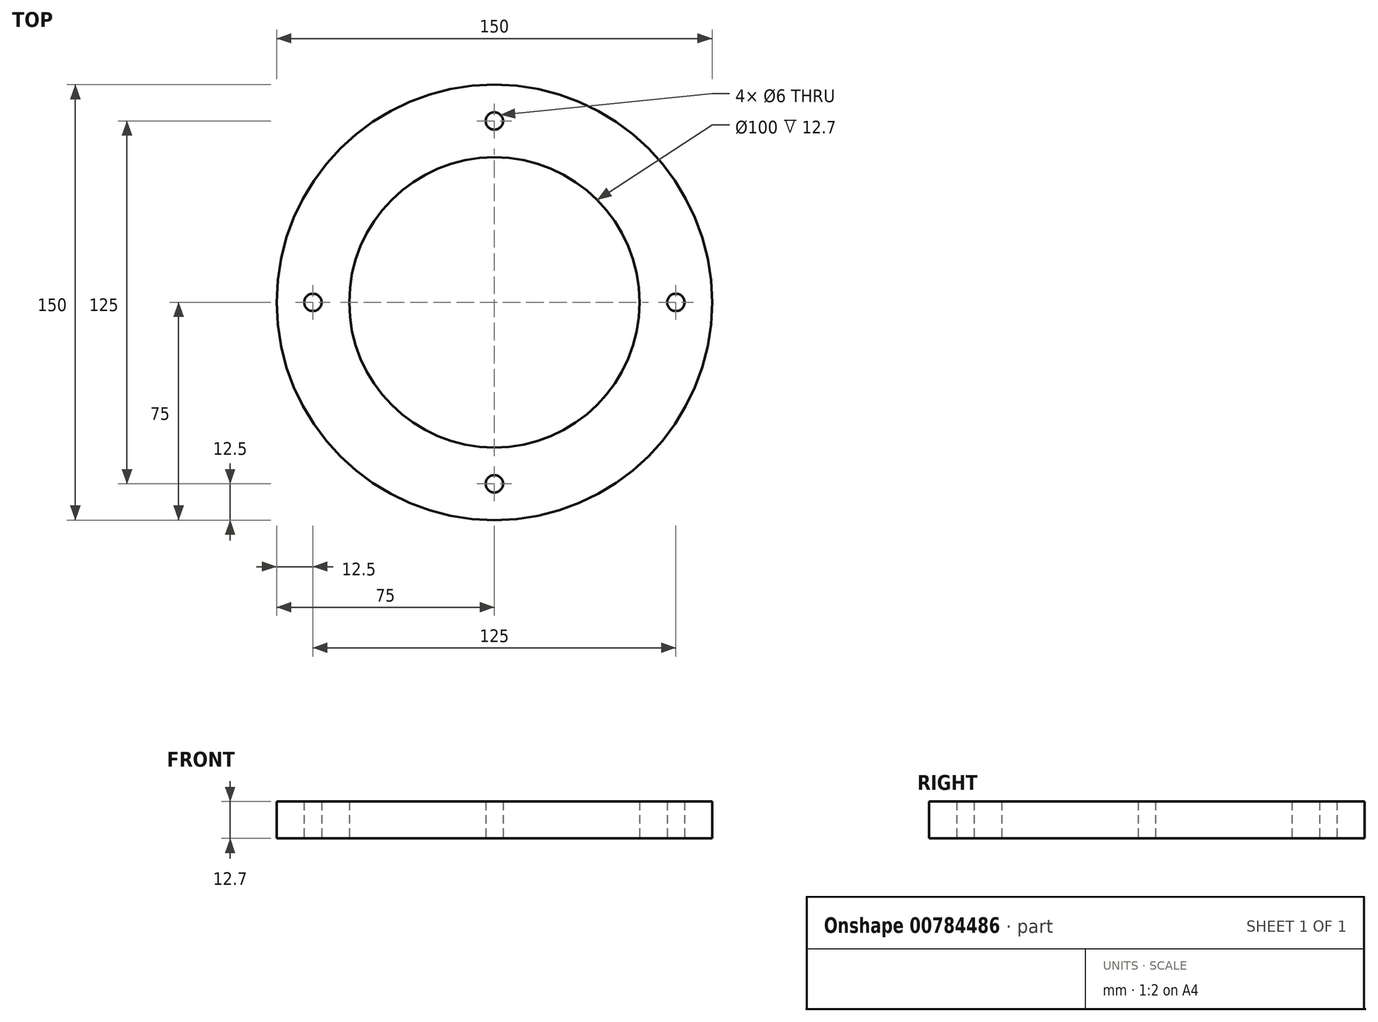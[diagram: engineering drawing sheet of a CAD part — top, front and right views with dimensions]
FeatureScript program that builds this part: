
annotation { "Feature Type Name" : "Feature", "Feature Type Description" : "" }
export const myFeature = defineFeature(function(context is Context, id is Id, definition is map)
    precondition{}
    {
        {
            var Q0;
            Q0=qCreatedBy(makeId("Top.planeOp"),FACE);
            var sketch = newSketch(context, id + "F0", { "sketchPlane" : qUnion([Q0])});
            skCircle(sketch, "E0", {"center": v(0, 0) * mm, "radius": 50 * mm});
            skCircle(sketch, "E1", {"center": v(0, 0) * mm, "radius": 75 * mm});
            skLineSegment(sketch, "E2", {"start": v(0, 0) * mm, "end": v(-62.5, 0) * mm});
            skLineSegment(sketch, "E3", {"start": v(0, 0) * mm, "end": v(0, 62.5) * mm});
            skLineSegment(sketch, "E4", {"start": v(0, 0) * mm, "end": v(62.5, 0) * mm});
            skLineSegment(sketch, "E5", {"start": v(0, 0) * mm, "end": v(0, -62.5) * mm});
            skCircle(sketch, "E6", {"center": v(-62.5, 0) * mm, "radius": 3 * mm});
            skCircle(sketch, "E7", {"center": v(0, 62.5) * mm, "radius": 3 * mm});
            skCircle(sketch, "E8", {"center": v(62.5, 0) * mm, "radius": 3 * mm});
            skCircle(sketch, "E9", {"center": v(0, -62.5) * mm, "radius": 3 * mm});
            skSolve(sketch);
        }
        {
            var Q0;
            Q0=makeQuery(id+"F0.imprint","IMPRINT",FACE,{"disambiguationData":[TD([[makeQuery(id+"F0.imprint","IMPRINT",EDGE,{"derivedFrom":sQuery(id+"F0.wireOp",EDGE,"E1")}),1.0]])]});
            extrude(context, id + "F1", {"entities" : qUnion([Q0]), "depth" : 12.7 * mm, "offsetDistance" : 25.4 * mm});
        }
    });
